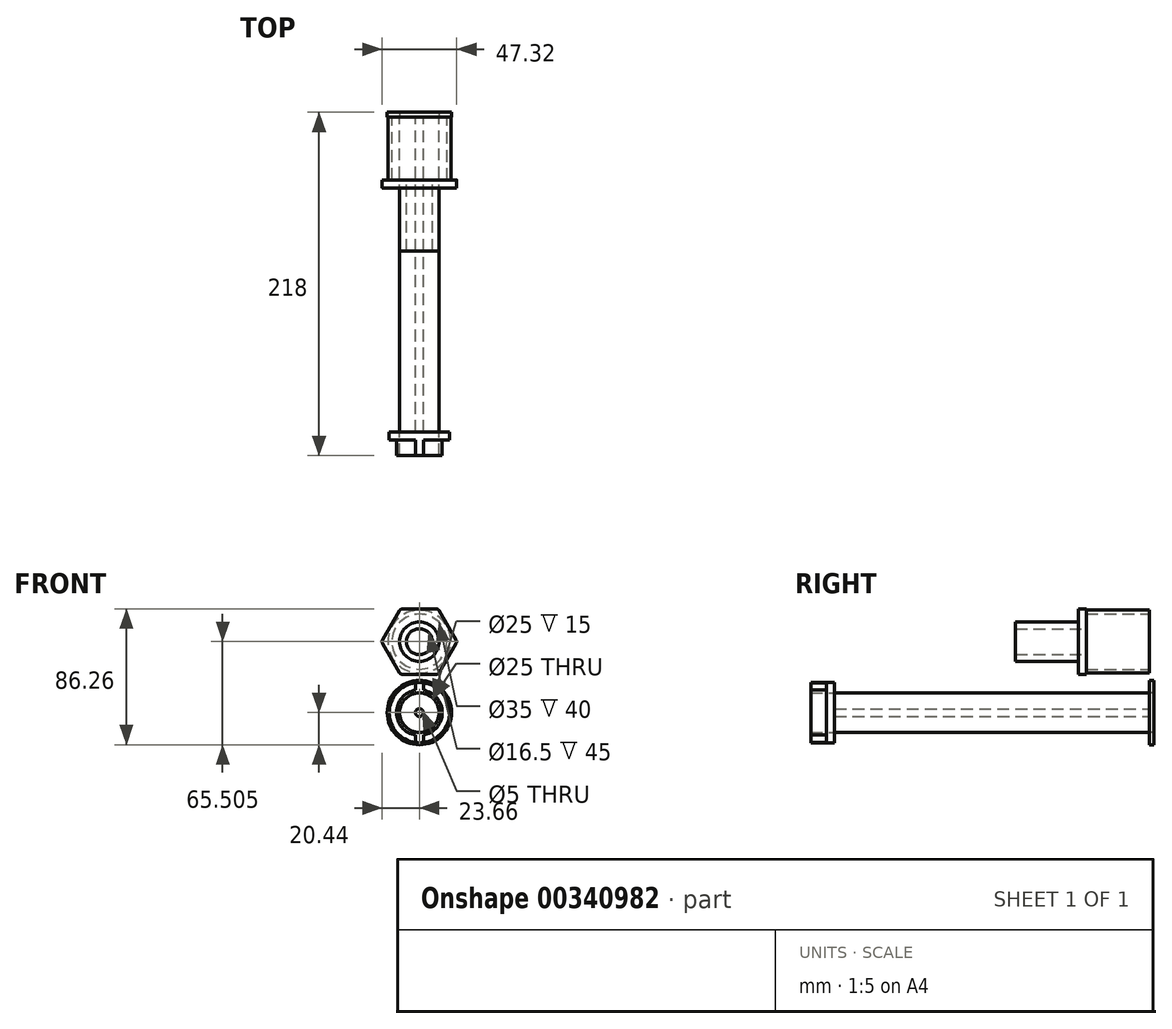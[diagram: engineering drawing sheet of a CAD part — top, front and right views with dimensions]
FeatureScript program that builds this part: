
annotation { "Feature Type Name" : "Feature", "Feature Type Description" : "" }
export const myFeature = defineFeature(function(context is Context, id is Id, definition is map)
    precondition{}
    {
        {
            var Q0;
            Q0=qCreatedBy(makeId("Front.planeOp"),FACE);
            var sketch = newSketch(context, id + "F0", { "sketchPlane" : qUnion([Q0])});
            skCircle(sketch, "E0", {"center": v(0, 0) * mm, "radius": 12.5 * mm});
            skCircle(sketch, "E1", {"center": v(0, 0) * mm, "radius": 2.5 * mm});
            skSolve(sketch);
        }
        {
            var Q0;
            Q0=makeQuery(id+"F0.imprint","IMPRINT",FACE,{"disambiguationData":[TD([[makeQuery(id+"F0.imprint","IMPRINT",EDGE,{"derivedFrom":sQuery(id+"F0.wireOp",EDGE,"E0")}),1.0]])]});
            extrude(context, id + "F1", {"entities" : qUnion([Q0]), "depth" : 200 * mm});
        }
        {
            var Q0;
            Q0=makeQuery(id+"F1.opExtrude","CAP_FACE",FACE,{"disambiguationData":[OSD([sQuery(id+"F0.wireOp",EDGE,"E0"),sQuery(id+"F0.wireOp",EDGE,"E1")])],"isStart":false});
            var sketch = newSketch(context, id + "F2", { "sketchPlane" : qUnion([Q0])});
            skCircle(sketch, "E2", {"center": v(0, 0) * mm, "radius": 12.5 * mm});
            skCircle(sketch, "E3", {"center": v(0, 0) * mm, "radius": 19.12 * mm});
            skSolve(sketch);
        }
        {
            var Q0;
            Q0=makeQuery(id+"F2.imprint","IMPRINT",FACE,{"disambiguationData":[TD([[makeQuery(id+"F2.imprint","IMPRINT",EDGE,{"derivedFrom":sQuery(id+"F2.wireOp",EDGE,"E2")}),-1.0]])]});
            extrude(context, id + "F3", {"entities" : qUnion([Q0]), "depth" : 5 * mm});
        }
        {
            var Q0;
            Q0=makeQuery(id+"F3.opExtrude","CAP_FACE",FACE,{"disambiguationData":[OSD([sQuery(id+"F2.wireOp",EDGE,"E2"),sQuery(id+"F2.wireOp",EDGE,"E3")])],"isStart":false});
            var sketch = newSketch(context, id + "F4", { "sketchPlane" : qUnion([Q0])});
            skCircle(sketch, "E4", {"center": v(0, 0) * mm, "radius": 19.12 * mm});
            skCircle(sketch, "E5", {"center": v(0, 0) * mm, "radius": 12.5 * mm});
            skCircle(sketch, "E6", {"center": v(0, 0) * mm, "radius": 14.5 * mm});
            skLineSegment(sketch, "E7", {"start": v(-2.5, 14.28) * mm, "end": v(-2.5, 18.95) * mm});
            skLineSegment(sketch, "E8", {"start": v(2.5, 14.28) * mm, "end": v(2.5, 18.95) * mm});
            skLineSegment(sketch, "E9", {"start": v(2.5, -14.28) * mm, "end": v(2.5, -18.95) * mm});
            skLineSegment(sketch, "E10", {"start": v(-2.5, -14.28) * mm, "end": v(-2.5, -18.95) * mm});
            skLineSegment(sketch, "E11", {"start": v(-2.5, 16.62) * mm, "end": v(0, 16.62) * mm, "construction": true});
            skLineSegment(sketch, "E12", {"start": v(0, 16.62) * mm, "end": v(2.5, 16.62) * mm, "construction": true});
            skLineSegment(sketch, "E13", {"start": v(-2.5, -16.62) * mm, "end": v(0, -16.62) * mm, "construction": true});
            skLineSegment(sketch, "E14", {"start": v(0, -16.62) * mm, "end": v(2.5, -16.62) * mm, "construction": true});
            skLineSegment(sketch, "E15", {"start": v(-2.5, -14.28) * mm, "end": v(-2.5, 14.28) * mm, "construction": true});
            skSolve(sketch);
        }
        {
            var Q0;
            {var subQ0=sQuery(id+"F4.wireOp",EDGE,"E7");Q0=makeQuery(id+"F4.imprint","IMPRINT",FACE,{"disambiguationData":[TD([[makeQuery(id+"F4.imprint","IMPRINT",EDGE,{"derivedFrom":subQ0}),-1.0]])]});}
            var Q1;
            {var subQ0=sQuery(id+"F4.wireOp",EDGE,"E9");Q1=makeQuery(id+"F4.imprint","IMPRINT",FACE,{"disambiguationData":[TD([[makeQuery(id+"F4.imprint","IMPRINT",EDGE,{"derivedFrom":subQ0}),-1.0]])]});}
            var Q2;
            Q2=makeQuery(id+"F4.imprint","IMPRINT",FACE,{"disambiguationData":[TD([[makeQuery(id+"F4.imprint","IMPRINT",EDGE,{"derivedFrom":sQuery(id+"F4.wireOp",EDGE,"E5")}),-1.0]])]});
            extrude(context, id + "F5", {"entities" : qUnion([Q0, Q1, Q2]), "operationType" : NewBodyOperationType.ADD, "depth" : 10 * mm});
        }
        {
            var Q0;
            Q0=qCreatedBy(makeId("Front.planeOp"),FACE);
            var sketch = newSketch(context, id + "F6", { "sketchPlane" : qUnion([Q0])});
            skCircle(sketch, "E16", {"center": v(0, 45.07) * mm, "radius": 17.5 * mm});
            skCircle(sketch, "E17", {"center": v(0, 45.07) * mm, "radius": 20 * mm});
            skSolve(sketch);
        }
        {
            var Q0;
            Q0=qSketchRegion(id+"F6",true);
            extrude(context, id + "F7", {"entities" : qUnion([Q0]), "depth" : 40 * mm});
        }
        {
            var Q0;
            Q0=makeQuery(id+"F7.opExtrude","CAP_FACE",FACE,{"disambiguationData":[OSD([sQuery(id+"F6.wireOp",EDGE,"E16"),sQuery(id+"F6.wireOp",EDGE,"E17")])],"isStart":false});
            var sketch = newSketch(context, id + "F8", { "sketchPlane" : qUnion([Q0])});
            skCircle(sketch, "E18.cCircle", {"center": v(0, 45.07) * mm, "radius": 20.76 * mm, "construction": true});
            skLineSegment(sketch, "E18.0", {"start": v(-10.83, 65.82) * mm, "end": v(10.83, 65.82) * mm});
            skLineSegment(sketch, "E18.1", {"start": v(12.56, 64.82) * mm, "end": v(23.4, 46.07) * mm});
            skLineSegment(sketch, "E18.2", {"start": v(23.4, 44.07) * mm, "end": v(12.56, 25.3) * mm});
            skLineSegment(sketch, "E18.3", {"start": v(10.83, 24.3) * mm, "end": v(-10.83, 24.3) * mm});
            skLineSegment(sketch, "E18.4", {"start": v(-12.56, 25.3) * mm, "end": v(-23.4, 44.07) * mm});
            skLineSegment(sketch, "E18.5", {"start": v(-23.4, 46.07) * mm, "end": v(-12.56, 64.82) * mm});
            skPoint(sketch, "E18.0.midPoint", {"position": v(0, 65.82) * mm});
            skCircle(sketch, "E19", {"center": v(0, 45.07) * mm, "radius": 8.25 * mm});
            skPoint(sketch, "E20.visualSharp", {"position": v(-23.97, 45.07) * mm});
            skArc(sketch, "E20.filletArc", {"start": v(-23.4, 46.07) * mm, "mid": v(-23.66, 45.07) * mm, "end": v(-23.4, 44.07) * mm});
            skPoint(sketch, "E21.visualSharp", {"position": v(-11.98, 24.3) * mm});
            skArc(sketch, "E21.filletArc", {"start": v(-12.56, 25.3) * mm, "mid": v(-11.83, 24.58) * mm, "end": v(-10.83, 24.3) * mm});
            skPoint(sketch, "E22.visualSharp", {"position": v(11.98, 24.3) * mm});
            skArc(sketch, "E22.filletArc", {"start": v(10.83, 24.3) * mm, "mid": v(11.83, 24.58) * mm, "end": v(12.56, 25.3) * mm});
            skPoint(sketch, "E23.visualSharp", {"position": v(23.97, 45.07) * mm});
            skArc(sketch, "E23.filletArc", {"start": v(23.4, 44.07) * mm, "mid": v(23.66, 45.07) * mm, "end": v(23.4, 46.07) * mm});
            skPoint(sketch, "E24.visualSharp", {"position": v(11.98, 65.82) * mm});
            skArc(sketch, "E24.filletArc", {"start": v(12.56, 64.82) * mm, "mid": v(11.83, 65.55) * mm, "end": v(10.83, 65.82) * mm});
            skPoint(sketch, "E25.visualSharp", {"position": v(-11.98, 65.82) * mm});
            skArc(sketch, "E25.filletArc", {"start": v(-10.83, 65.82) * mm, "mid": v(-11.83, 65.55) * mm, "end": v(-12.56, 64.82) * mm});
            skSolve(sketch);
        }
        {
            var Q0;
            Q0=qSketchRegion(id+"F8",true);
            extrude(context, id + "F9", {"entities" : qUnion([Q0]), "operationType" : NewBodyOperationType.ADD, "depth" : 5 * mm});
        }
        {
            var Q0;
            Q0=makeQuery(id+"F9.opExtrude","CAP_FACE",FACE,{"disambiguationData":[OSD([sQuery(id+"F8.wireOp",EDGE,"E18.0"),sQuery(id+"F8.wireOp",EDGE,"E18.1"),sQuery(id+"F8.wireOp",EDGE,"E18.2"),sQuery(id+"F8.wireOp",EDGE,"E18.3"),sQuery(id+"F8.wireOp",EDGE,"E18.4"),sQuery(id+"F8.wireOp",EDGE,"E18.5"),sQuery(id+"F8.wireOp",EDGE,"E19"),sQuery(id+"F8.wireOp",EDGE,"E20.filletArc"),sQuery(id+"F8.wireOp",EDGE,"E21.filletArc"),sQuery(id+"F8.wireOp",EDGE,"E22.filletArc"),sQuery(id+"F8.wireOp",EDGE,"E23.filletArc"),sQuery(id+"F8.wireOp",EDGE,"E24.filletArc"),sQuery(id+"F8.wireOp",EDGE,"E25.filletArc")])],"isStart":false});
            var sketch = newSketch(context, id + "F10", { "sketchPlane" : qUnion([Q0])});
            skCircle(sketch, "E26", {"center": v(0, 45.07) * mm, "radius": 8.25 * mm});
            skCircle(sketch, "E27", {"center": v(0, 45.07) * mm, "radius": 12.5 * mm});
            skSolve(sketch);
        }
        {
            var Q0;
            Q0=qSketchRegion(id+"F10",true);
            extrude(context, id + "F11", {"entities" : qUnion([Q0]), "operationType" : NewBodyOperationType.ADD, "depth" : 40 * mm});
        }
        {
            var Q0;
            Q0=makeQuery(id+"F1.opExtrude","CAP_FACE",FACE,{"disambiguationData":[OSD([sQuery(id+"F0.wireOp",EDGE,"E0"),sQuery(id+"F0.wireOp",EDGE,"E1")])],"isStart":true});
            var sketch = newSketch(context, id + "F12", { "sketchPlane" : qUnion([Q0])});
            skCircle(sketch, "E28", {"center": v(0, 0) * mm, "radius": 12.5 * mm});
            skCircle(sketch, "E29", {"center": v(0, 0) * mm, "radius": 20.44 * mm});
            skSolve(sketch);
        }
        {
            var Q0;
            Q0=qSketchRegion(id+"F12",true);
            extrude(context, id + "F13", {"entities" : qUnion([Q0]), "depth" : 3 * mm});
        }
    });
